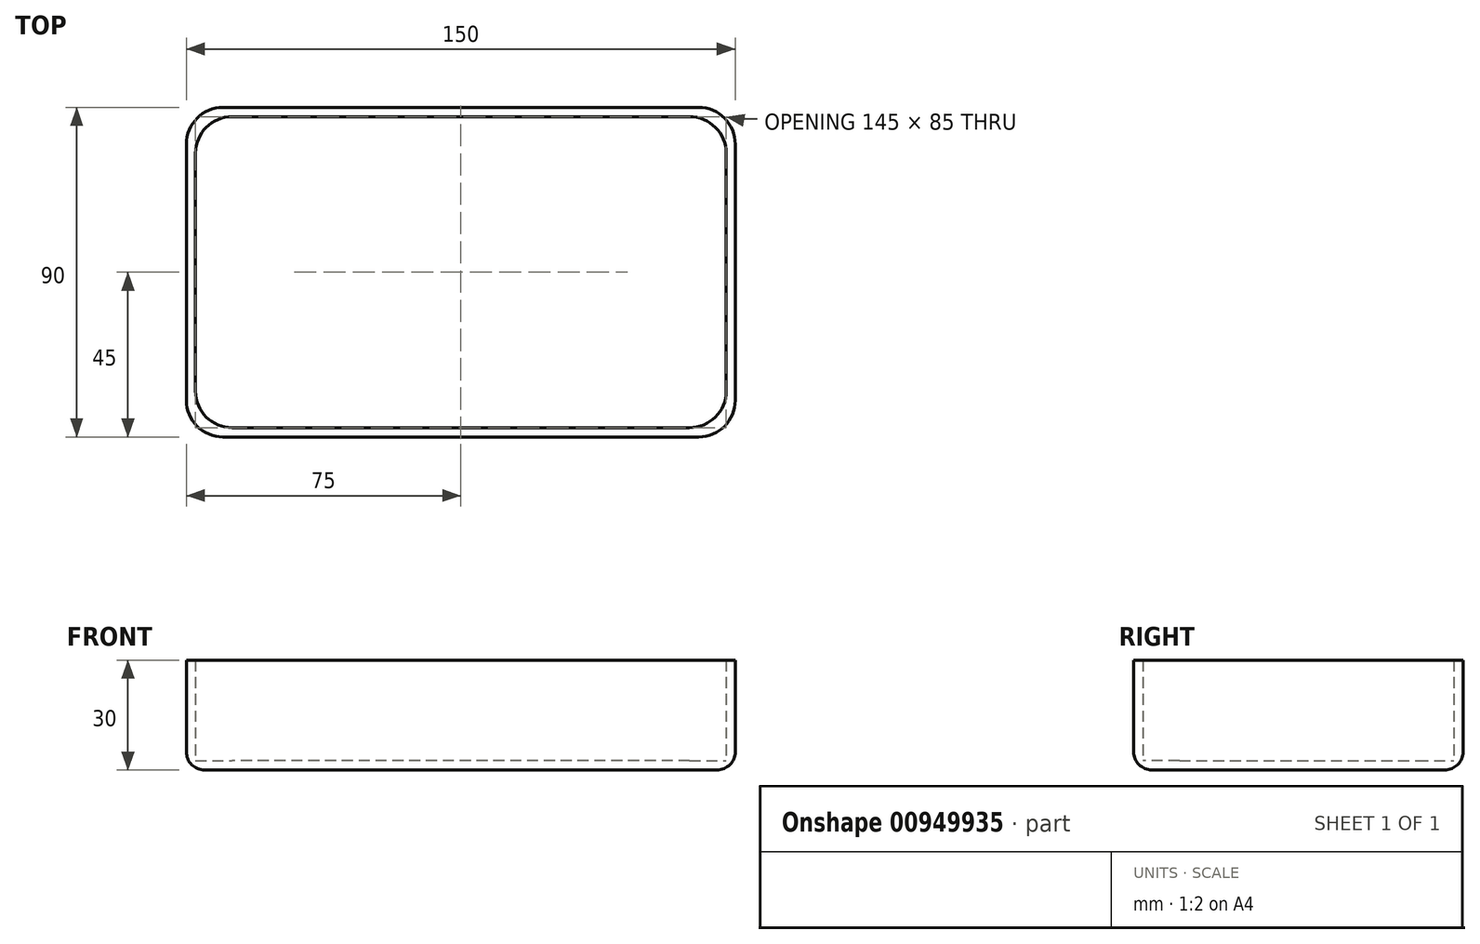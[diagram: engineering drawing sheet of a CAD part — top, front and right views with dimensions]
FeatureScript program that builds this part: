
annotation { "Feature Type Name" : "Feature", "Feature Type Description" : "" }
export const myFeature = defineFeature(function(context is Context, id is Id, definition is map)
    precondition{}
    {
        {
            var Q0;
            Q0=qCreatedBy(makeId("Top.planeOp"),FACE);
            var sketch = newSketch(context, id + "F0", { "sketchPlane" : qUnion([Q0])});
            skLineSegment(sketch, "E0.bottom", {"start": v(75, -45) * mm, "end": v(-75, -45) * mm});
            skLineSegment(sketch, "E0.top", {"start": v(75, 45) * mm, "end": v(-75, 45) * mm});
            skLineSegment(sketch, "E0.left", {"start": v(75, -45) * mm, "end": v(75, 45) * mm});
            skLineSegment(sketch, "E0.right", {"start": v(-75, -45) * mm, "end": v(-75, 45) * mm});
            skPoint(sketch, "E0.middle", {"position": v(0, 0) * mm});
            skSolve(sketch);
        }
        {
            var Q0;
            Q0 = qSketchRegion(id + "F0", true);
            extrude(context, id + "F1", {"entities" : qUnion([Q0]), "depth" : 30 * mm, "offsetDistance" : 25 * mm});
        }
        {
            var Q0;
            Q0=makeQuery(id+"F1.opExtrude","CAP_FACE",FACE,{"disambiguationData":[OSD([sQuery(id+"F0.wireOp",EDGE,"E0.bottom"),sQuery(id+"F0.wireOp",EDGE,"E0.top"),sQuery(id+"F0.wireOp",EDGE,"E0.left"),sQuery(id+"F0.wireOp",EDGE,"E0.right")])],"isStart":false});
            shell(context, id + "F2", {"entities" : qUnion([Q0]), "thickness" : 2.5 * mm});
        }
        {
            var Q0;
            Q0=makeQuery(id+"F1.opExtrude","SWEPT_EDGE",EDGE,{"disambiguationData":[OSD([sQuery(id+"F0.wireOp",EDGE,"E0.top"),sQuery(id+"F0.wireOp",EDGE,"E0.right")])]});
            var Q1;
            Q1=makeQuery(id+"F1.opExtrude","SWEPT_EDGE",EDGE,{"disambiguationData":[OSD([sQuery(id+"F0.wireOp",EDGE,"E0.top"),sQuery(id+"F0.wireOp",EDGE,"E0.left")])]});
            var Q2;
            Q2=makeQuery(id+"F1.opExtrude","SWEPT_EDGE",EDGE,{"disambiguationData":[OSD([sQuery(id+"F0.wireOp",EDGE,"E0.bottom"),sQuery(id+"F0.wireOp",EDGE,"E0.left")])]});
            var Q3;
            Q3=makeQuery(id+"F1.opExtrude","SWEPT_EDGE",EDGE,{"disambiguationData":[OSD([sQuery(id+"F0.wireOp",EDGE,"E0.bottom"),sQuery(id+"F0.wireOp",EDGE,"E0.right")])]});
            var Q4;
            Q4=makeQuery(id+"F2.opShell","OFFSET_EDGE",EDGE,{"disambiguationData":[OSD([sQuery(id+"F0.wireOp",EDGE,"E0.top"),sQuery(id+"F0.wireOp",EDGE,"E0.right")])]});
            var Q5;
            Q5=makeQuery(id+"F2.opShell","OFFSET_EDGE",EDGE,{"disambiguationData":[OSD([sQuery(id+"F0.wireOp",EDGE,"E0.top"),sQuery(id+"F0.wireOp",EDGE,"E0.left")])]});
            var Q6;
            Q6=makeQuery(id+"F2.opShell","OFFSET_EDGE",EDGE,{"disambiguationData":[OSD([sQuery(id+"F0.wireOp",EDGE,"E0.bottom"),sQuery(id+"F0.wireOp",EDGE,"E0.left")])]});
            var Q7;
            Q7=makeQuery(id+"F2.opShell","OFFSET_EDGE",EDGE,{"disambiguationData":[OSD([sQuery(id+"F0.wireOp",EDGE,"E0.bottom"),sQuery(id+"F0.wireOp",EDGE,"E0.right")])]});
            fillet(context, id + "F3", {"entities" : qUnion([Q0, Q1, Q2, Q3, Q4, Q5, Q6, Q7]), "radius" : 10 * mm, "tangentPropagation" : true, "allowEdgeOverflow" : false});
        }
        {
            var Q0;
            Q0=makeQuery(id+"F1.opExtrude","CAP_EDGE",EDGE,{"disambiguationData":[OSD([sQuery(id+"F0.wireOp",EDGE,"E0.right")])],"isStart":true});
            var Q1;
            {var subQ0=sQuery(id+"F0.wireOp",EDGE,"E0.right");var subQ1=sQuery(id+"F0.wireOp",EDGE,"E0.bottom");Q1=makeQuery(id+"F3.opFillet","BLEND_EDGE",EDGE,{"blendedFrom":[makeQuery(id+"F1.opExtrude","SWEPT_EDGE",EDGE,{"disambiguationData":[OSD([subQ1,subQ0])]}),makeQuery(id+"F1.opExtrude","CAP_FACE",FACE,{"disambiguationData":[OSD([subQ1,sQuery(id+"F0.wireOp",EDGE,"E0.top"),sQuery(id+"F0.wireOp",EDGE,"E0.left"),subQ0])],"isStart":true})],"blendedInto":[makeQuery(id+"F1.opExtrude","CAP_FACE",FACE,{"disambiguationData":[OSD([subQ1,sQuery(id+"F0.wireOp",EDGE,"E0.top"),sQuery(id+"F0.wireOp",EDGE,"E0.left"),subQ0])],"isStart":true})]});}
            var Q2;
            Q2=makeQuery(id+"F1.opExtrude","CAP_EDGE",EDGE,{"disambiguationData":[OSD([sQuery(id+"F0.wireOp",EDGE,"E0.bottom")])],"isStart":true});
            var Q3;
            {var subQ0=sQuery(id+"F0.wireOp",EDGE,"E0.left");var subQ1=sQuery(id+"F0.wireOp",EDGE,"E0.bottom");Q3=makeQuery(id+"F3.opFillet","BLEND_EDGE",EDGE,{"blendedFrom":[makeQuery(id+"F1.opExtrude","SWEPT_EDGE",EDGE,{"disambiguationData":[OSD([subQ1,subQ0])]}),makeQuery(id+"F1.opExtrude","CAP_FACE",FACE,{"disambiguationData":[OSD([subQ1,sQuery(id+"F0.wireOp",EDGE,"E0.top"),subQ0,sQuery(id+"F0.wireOp",EDGE,"E0.right")])],"isStart":true})],"blendedInto":[makeQuery(id+"F1.opExtrude","CAP_FACE",FACE,{"disambiguationData":[OSD([subQ1,sQuery(id+"F0.wireOp",EDGE,"E0.top"),subQ0,sQuery(id+"F0.wireOp",EDGE,"E0.right")])],"isStart":true})]});}
            var Q4;
            Q4=makeQuery(id+"F1.opExtrude","CAP_EDGE",EDGE,{"disambiguationData":[OSD([sQuery(id+"F0.wireOp",EDGE,"E0.left")])],"isStart":true});
            var Q5;
            {var subQ0=sQuery(id+"F0.wireOp",EDGE,"E0.left");var subQ1=sQuery(id+"F0.wireOp",EDGE,"E0.top");Q5=makeQuery(id+"F3.opFillet","BLEND_EDGE",EDGE,{"blendedFrom":[makeQuery(id+"F1.opExtrude","SWEPT_EDGE",EDGE,{"disambiguationData":[OSD([subQ1,subQ0])]}),makeQuery(id+"F1.opExtrude","CAP_FACE",FACE,{"disambiguationData":[OSD([sQuery(id+"F0.wireOp",EDGE,"E0.bottom"),subQ1,subQ0,sQuery(id+"F0.wireOp",EDGE,"E0.right")])],"isStart":true})],"blendedInto":[makeQuery(id+"F1.opExtrude","CAP_FACE",FACE,{"disambiguationData":[OSD([sQuery(id+"F0.wireOp",EDGE,"E0.bottom"),subQ1,subQ0,sQuery(id+"F0.wireOp",EDGE,"E0.right")])],"isStart":true})]});}
            var Q6;
            Q6=makeQuery(id+"F1.opExtrude","CAP_EDGE",EDGE,{"disambiguationData":[OSD([sQuery(id+"F0.wireOp",EDGE,"E0.top")])],"isStart":true});
            var Q7;
            {var subQ0=sQuery(id+"F0.wireOp",EDGE,"E0.right");var subQ1=sQuery(id+"F0.wireOp",EDGE,"E0.top");Q7=makeQuery(id+"F3.opFillet","BLEND_EDGE",EDGE,{"blendedFrom":[makeQuery(id+"F1.opExtrude","SWEPT_EDGE",EDGE,{"disambiguationData":[OSD([subQ1,subQ0])]}),makeQuery(id+"F1.opExtrude","CAP_FACE",FACE,{"disambiguationData":[OSD([sQuery(id+"F0.wireOp",EDGE,"E0.bottom"),subQ1,sQuery(id+"F0.wireOp",EDGE,"E0.left"),subQ0])],"isStart":true})],"blendedInto":[makeQuery(id+"F1.opExtrude","CAP_FACE",FACE,{"disambiguationData":[OSD([sQuery(id+"F0.wireOp",EDGE,"E0.bottom"),subQ1,sQuery(id+"F0.wireOp",EDGE,"E0.left"),subQ0])],"isStart":true})]});}
            fillet(context, id + "F4", {"entities" : qUnion([Q0, Q1, Q2, Q3, Q4, Q5, Q6, Q7]), "radius" : 5 * mm, "tangentPropagation" : true, "allowEdgeOverflow" : false});
        }
    });
